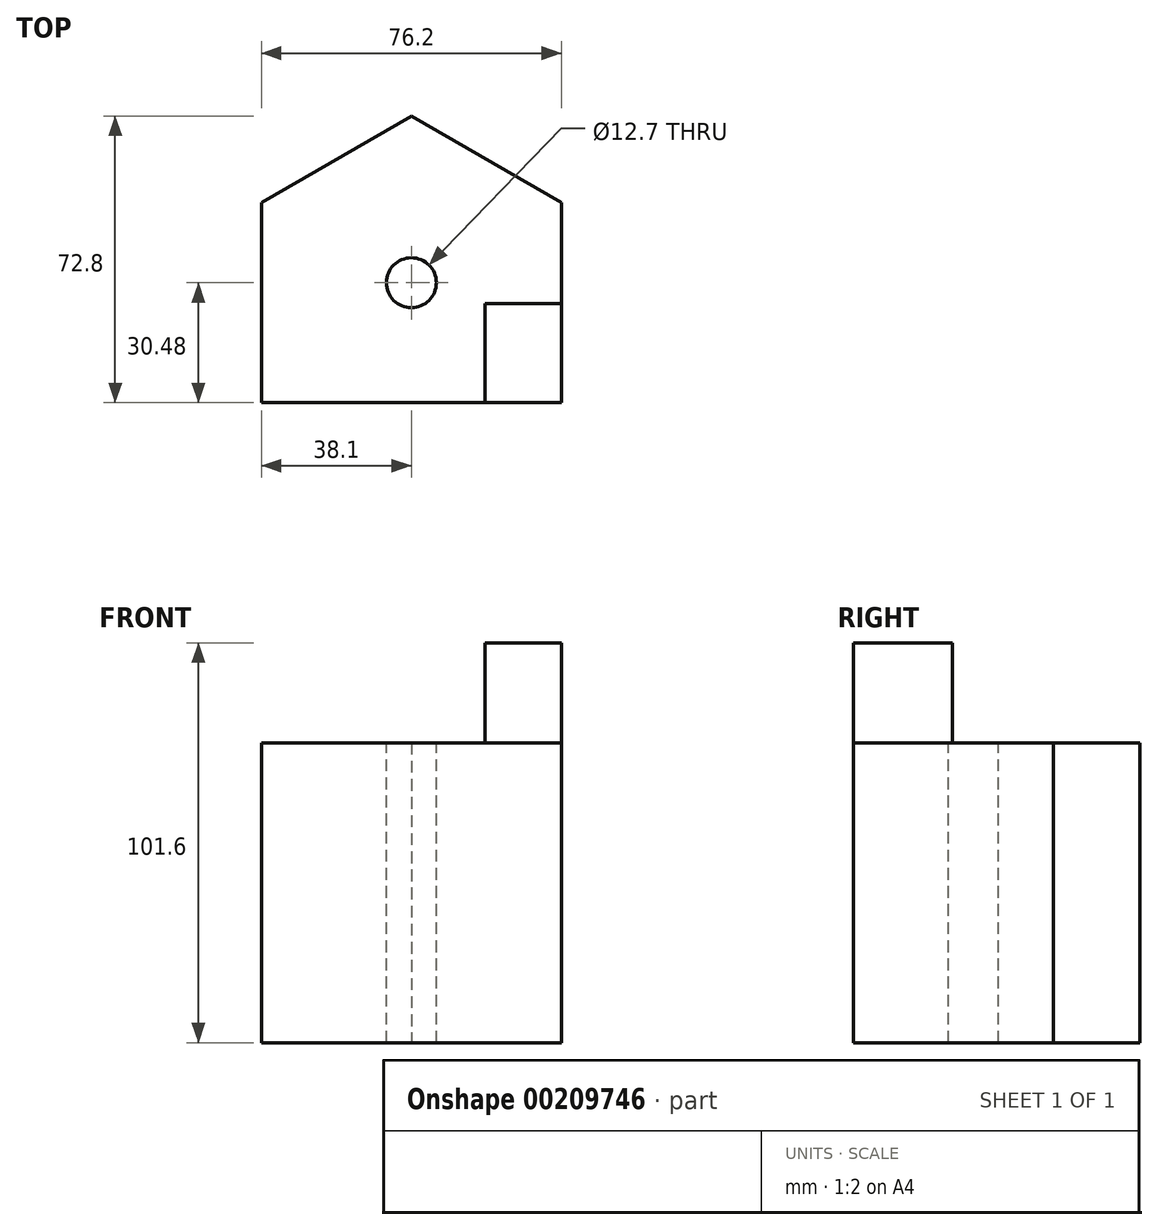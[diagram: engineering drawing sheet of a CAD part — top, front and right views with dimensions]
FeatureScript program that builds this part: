
annotation { "Feature Type Name" : "Feature", "Feature Type Description" : "" }
export const myFeature = defineFeature(function(context is Context, id is Id, definition is map)
    precondition{}
    {
        {
            var Q0;
            Q0=qCreatedBy(makeId("Top.planeOp"),FACE);
            var sketch = newSketch(context, id + "F0", { "sketchPlane" : qUnion([Q0])});
            skLineSegment(sketch, "E0.bottom", {"start": v(0, 0) * mm, "end": v(76.2, 0) * mm});
            skLineSegment(sketch, "E0.top", {"start": v(0, 50.8) * mm, "end": v(76.2, 50.8) * mm});
            skLineSegment(sketch, "E0.left", {"start": v(0, 0) * mm, "end": v(0, 50.8) * mm});
            skLineSegment(sketch, "E0.right", {"start": v(76.2, 0) * mm, "end": v(76.2, 50.8) * mm});
            skLineSegment(sketch, "E1", {"start": v(0, 50.8) * mm, "end": v(38.1, 72.8) * mm});
            skLineSegment(sketch, "E2", {"start": v(38.1, 72.8) * mm, "end": v(76.2, 50.8) * mm});
            skPoint(sketch, "E3", {"position": v(38.1, 50.8) * mm});
            skSolve(sketch);
        }
        {
            var Q0;
            Q0 = qSketchRegion(id + "F0", true);
            extrude(context, id + "F1", {"entities" : qUnion([Q0]), "depth" : 76.2 * mm});
        }
        {
            var Q0;
            Q0=makeQuery(id+"F1.opExtrude","CAP_FACE",FACE,{"disambiguationData":[OSD([sQuery(id+"F0.wireOp",EDGE,"E0.bottom"),sQuery(id+"F0.wireOp",EDGE,"E0.left"),sQuery(id+"F0.wireOp",EDGE,"E0.right"),sQuery(id+"F0.wireOp",EDGE,"E1"),sQuery(id+"F0.wireOp",EDGE,"E2")])],"isStart":false});
            var sketch = newSketch(context, id + "F2", { "sketchPlane" : qUnion([Q0])});
            skCircle(sketch, "E4", {"center": v(38.1, 30.48) * mm, "radius": 6.35 * mm});
            skSolve(sketch);
        }
        {
            var Q0;
            Q0=makeQuery(id+"F2.imprint","IMPRINT",FACE,{"disambiguationData":[TD([[makeQuery(id+"F2.imprint","IMPRINT",EDGE,{"derivedFrom":sQuery(id+"F2.wireOp",EDGE,"E4")}),1.0]])]});
            extrude(context, id + "F3", {"entities" : qUnion([Q0]), "operationType" : NewBodyOperationType.REMOVE, "endBound" : BoundingType.THROUGH_ALL, "oppositeDirection" : true, "depth" : 25.4 * mm});
        }
        {
            var Q0;
            Q0=makeQuery(id+"F1.opExtrude","CAP_FACE",FACE,{"disambiguationData":[OSD([sQuery(id+"F0.wireOp",EDGE,"E0.bottom"),sQuery(id+"F0.wireOp",EDGE,"E0.left"),sQuery(id+"F0.wireOp",EDGE,"E0.right"),sQuery(id+"F0.wireOp",EDGE,"E1"),sQuery(id+"F0.wireOp",EDGE,"E2")])],"isStart":false});
            var sketch = newSketch(context, id + "F4", { "sketchPlane" : qUnion([Q0])});
            skLineSegment(sketch, "E5.bottom", {"start": v(76.2, 0) * mm, "end": v(56.86, 0) * mm});
            skLineSegment(sketch, "E5.top", {"start": v(76.2, 25.14) * mm, "end": v(56.86, 25.14) * mm});
            skLineSegment(sketch, "E5.left", {"start": v(76.2, 0) * mm, "end": v(76.2, 25.14) * mm});
            skLineSegment(sketch, "E5.right", {"start": v(56.86, 0) * mm, "end": v(56.86, 25.14) * mm});
            skSolve(sketch);
        }
        {
            var Q0;
            Q0 = qSketchRegion(id + "F4", true);
            extrude(context, id + "F5", {"entities" : qUnion([Q0]), "depth" : 25.4 * mm});
        }
    });
